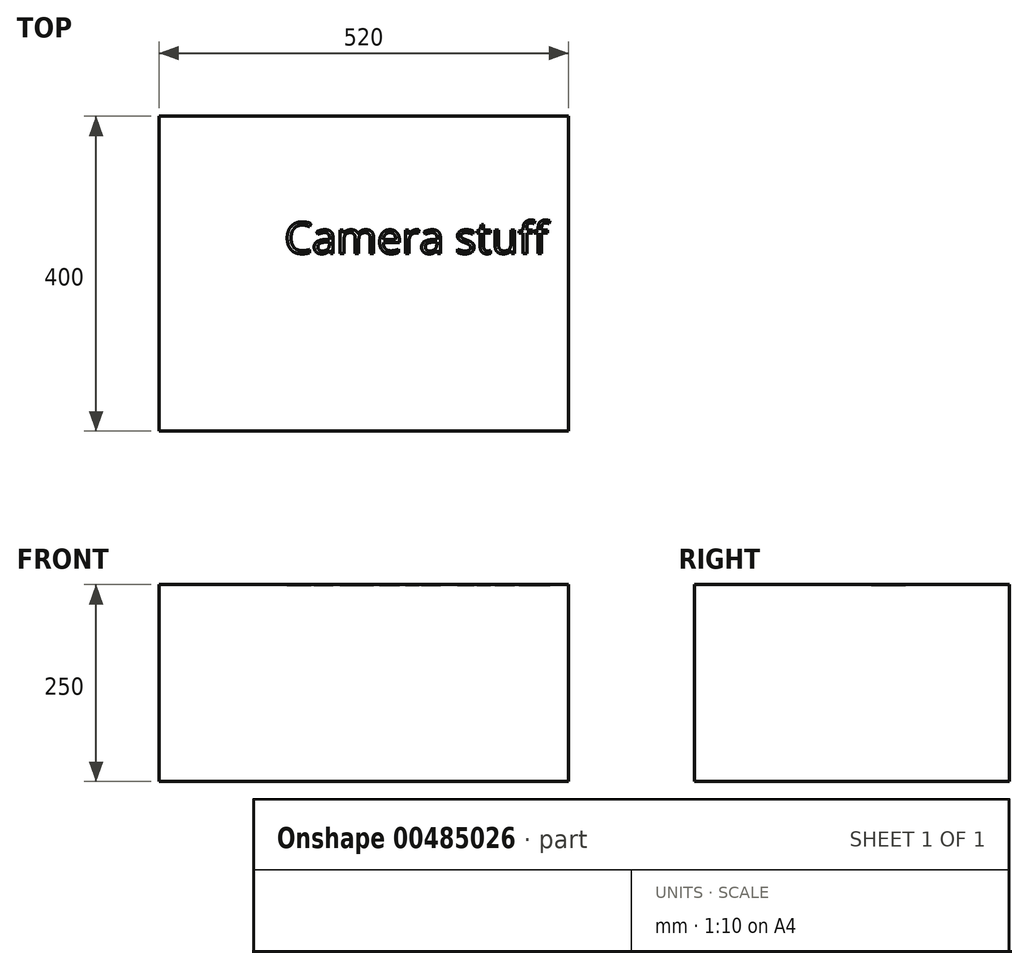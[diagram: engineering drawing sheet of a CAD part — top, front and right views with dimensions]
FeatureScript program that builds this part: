
annotation { "Feature Type Name" : "Feature", "Feature Type Description" : "" }
export const myFeature = defineFeature(function(context is Context, id is Id, definition is map)
    precondition{}
    {
        {
            var Q0;
            Q0=qCreatedBy(makeId("Top.planeOp"),FACE);
            var sketch = newSketch(context, id + "F0", { "sketchPlane" : qUnion([Q0])});
            skLineSegment(sketch, "E0.bottom", {"start": v(260, -200) * mm, "end": v(-260, -200) * mm});
            skLineSegment(sketch, "E0.top", {"start": v(260, 200) * mm, "end": v(-260, 200) * mm});
            skLineSegment(sketch, "E0.left", {"start": v(260, -200) * mm, "end": v(260, 200) * mm});
            skLineSegment(sketch, "E0.right", {"start": v(-260, -200) * mm, "end": v(-260, 200) * mm});
            skPoint(sketch, "E0.middle", {"position": v(0, 0) * mm});
            skSolve(sketch);
        }
        {
            var Q0;
            Q0 = qSketchRegion(id + "F0", true);
            extrude(context, id + "F1", {"entities" : qUnion([Q0]), "depth" : 250 * mm, "offsetDistance" : 25 * mm});
        }
        {
            var Q0;
            Q0=makeQuery(id+"F1.opExtrude","CAP_FACE",FACE,{"disambiguationData":[OSD([sQuery(id+"F0.wireOp",EDGE,"E0.bottom"),sQuery(id+"F0.wireOp",EDGE,"E0.top"),sQuery(id+"F0.wireOp",EDGE,"E0.left"),sQuery(id+"F0.wireOp",EDGE,"E0.right")])],"isStart":false});
            var sketch = newSketch(context, id + "F2", { "sketchPlane" : qUnion([Q0])});
            skText(sketch, "E1", { "text": "Camera stuff", "fontName": "OpenSans-Regular.ttf"});
            const initialGuessF2  = {"E1": [-0.10058, 0.02556, 1, 0, 0.04]};
            skSetInitialGuess(sketch, initialGuessF2);
            skSolve(sketch);
        }
        {
            var Q0;
            Q0 = qSketchRegion(id + "F2", true);
            extrude(context, id + "F3", {"entities" : qUnion([Q0]), "operationType" : NewBodyOperationType.REMOVE, "oppositeDirection" : true, "depth" : 1 * mm, "offsetDistance" : 25 * mm});
        }
    });
